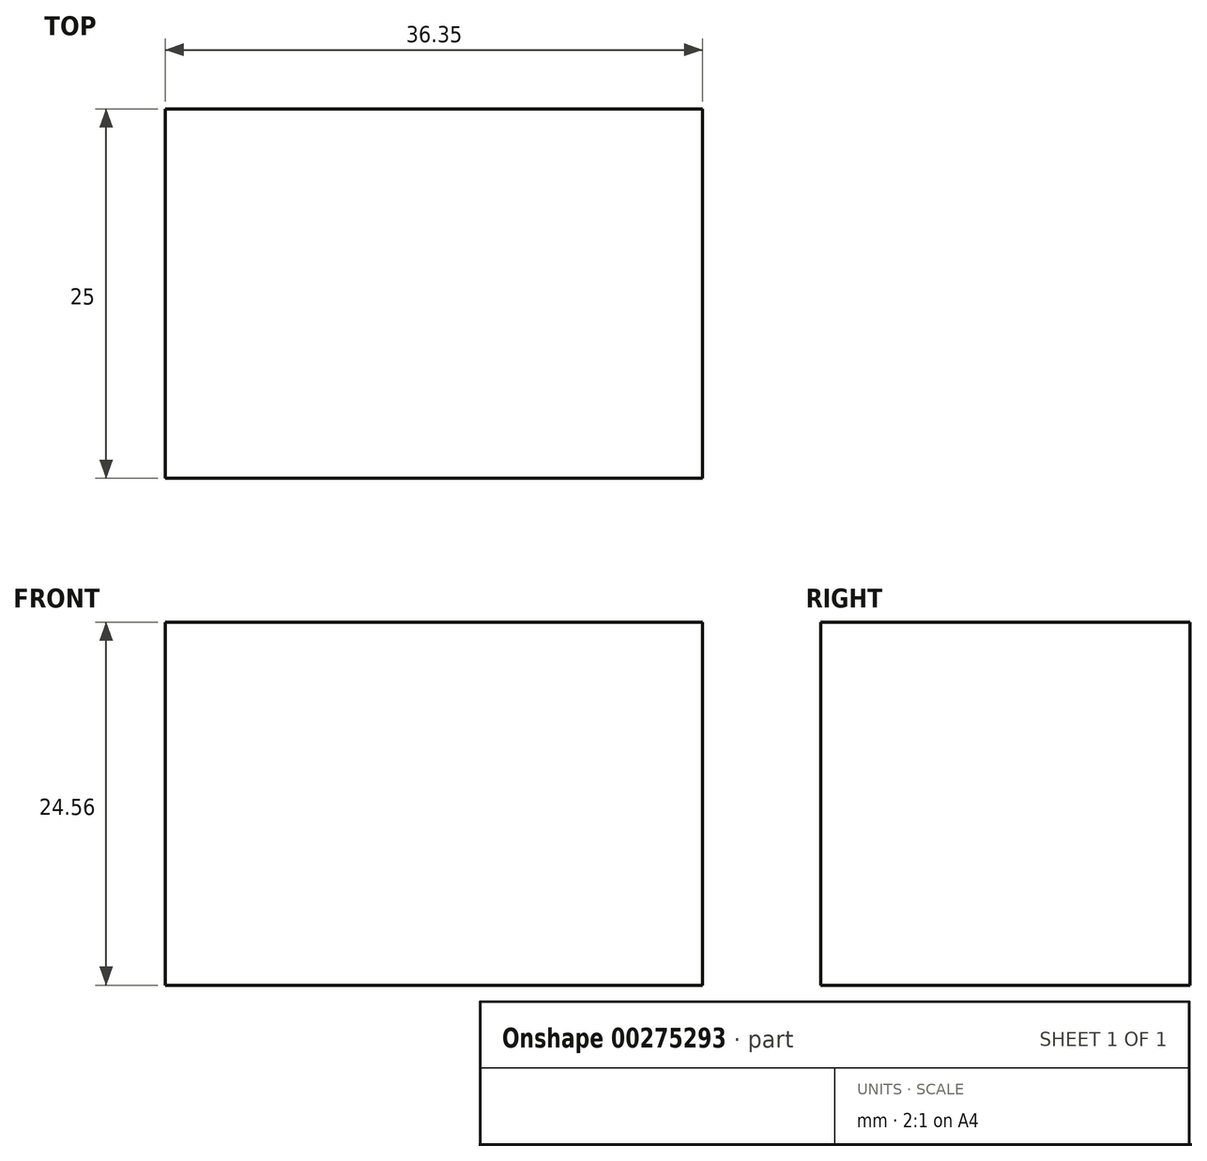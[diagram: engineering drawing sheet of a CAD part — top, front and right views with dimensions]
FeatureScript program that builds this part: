
annotation { "Feature Type Name" : "Feature", "Feature Type Description" : "" }
export const myFeature = defineFeature(function(context is Context, id is Id, definition is map)
    precondition{}
    {
        {
            var Q0;
            Q0=qCreatedBy(makeId("Front.planeOp"),FACE);
            var sketch = newSketch(context, id + "F0", { "sketchPlane" : qUnion([Q0])});
            skLineSegment(sketch, "E0.bottom", {"start": v(-29.86, 42.01) * mm, "end": v(-66.2, 42.01) * mm});
            skLineSegment(sketch, "E0.top", {"start": v(-29.86, 66.57) * mm, "end": v(-66.2, 66.57) * mm});
            skLineSegment(sketch, "E0.left", {"start": v(-29.86, 42.01) * mm, "end": v(-29.86, 66.57) * mm});
            skLineSegment(sketch, "E0.right", {"start": v(-66.2, 42.01) * mm, "end": v(-66.2, 66.57) * mm});
            skPoint(sketch, "E0.middle", {"position": v(-48.03, 54.3) * mm});
            skSolve(sketch);
        }
        {
            var Q0;
            Q0 = qSketchRegion(id + "F0", true);
            extrude(context, id + "F1", {"entities" : qUnion([Q0]), "depth" : 25 * mm});
        }
    });
